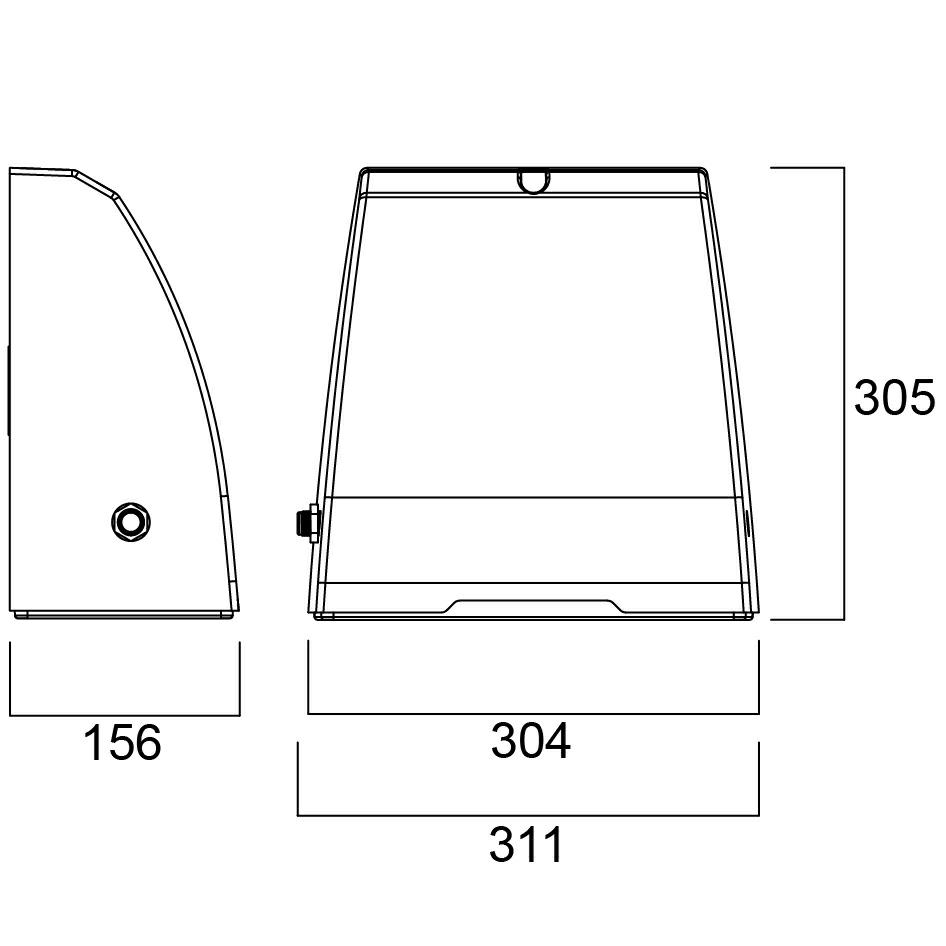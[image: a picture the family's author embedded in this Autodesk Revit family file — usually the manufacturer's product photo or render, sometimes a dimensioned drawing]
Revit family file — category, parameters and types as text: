
# Revit family: 0049944_3150lm
name_source: partatom
category: Lighting Fixtures
revit_build: Autodesk Revit 2018 (Build: 20170223_1515(x64)
units: mm (PartAtom-declared; Revit-internal decimal feet)

## family parameters
Cut with Voids When Loaded = No
Host = Face
Light Source = Yes
OmniClass Number = 23.80.70.00
OmniClass Title = Lighting
Part Type = Normal
Room Calculation Point = No
Round Connector Dimension = Use Diameter
Shared = No

## types (1)
- 0049944 MURO SURF IP65 1700-3250LM 840 PH GR
    Apparent Load = 28 VA
    Assembly Code = D5020200
    AssetType = Fixed
    ClassificationName = Uniclass2015
    ClassificationValue = EF_70_80
    Color Filter = 16777215
    Cost = 0 $
    Default Elevation = 1219 mm
    Description = Muro Surface is a wall mounted fixture for exterior lighting applications. Comes with aluminium housing in RAL7016 anthracite grey colour, frosted PC diffuser, IP65, IK10, Class I, 4000K, non-dimmable multipower driver with 5 settings, 1700 / 1900 / 2750 / 3150 / 3250 lm, 14 / 16 / 24 / 27 / 28 W, up to 121 lm/W total system efficacy, switchable built in Mini photocell, CRI80, Asymmetrical beam, 119.000 hrs L70B50 lifespan, 304 x 305 x 155 mm (L x W x D) dimensions, 4.1 kg weight.
    Dimming Lamp Color Temperature Shift = <None>
    DocumentationLiterature = http://www.sylvania-lighting.com
    ElectricShockClassification = 116
    Emit Shape Visible in Rendering = No
    Emit from Circle Diameter = 610 mm
    IfcExportAs = Class I
    IfcExportType = IfcLightFixtureType
    ImpactProtectionIndex = IfcLightFixtureType
    IngressProtection = IfcLightFixtureType
    InputNominalFrequency = 4000
    InputVoltage = 0
    LampColourRenderingIndex = 16500
    LampColourTemperature = LED
    LampMacAdamStep = 80
    LampNominalLuminous = 4000 K
    LightOutputRatio = LED
    LuminaireType = 0
    ManufacturerName = 116 lm/W
    Material = Feilo Sylvania
    Material_1_SYL = <By Category>
    Material_2_SYL = <By Category>
    Material_3_SYL = <By Category>
    Material_4_SYL = <By Category>
    Model = Muro Surface IP65 1700-3250lm 840 PH Grey
    ModelNumber = 0049944
    ModelReference = Muro Surface IP65 1700-3250lm 840 PH Grey
    Name = Muro Surface IP65 1700-3250lm 840 PH Grey
    NominalDepth = 155 mm  [stored 0.50853 ft]
    NominalHeight = 305 mm  [stored 1.00066 ft]
    NominalLength = 155 mm  [stored 0.50853 ft]
    Photometric Web File = 0049944_3150lm.IES
    PowerConsumption = Lighting
    PowerFactor = 0.95
    Tilt Angle = -90.00°
    Type Image = <None>
    TypeName = Muro Surface IP65 1700-3250lm 840 PH Grey
    URL = 0.9
    Voltage = 0 V
    WarrantyDescription = http://www.sylvania-lighting.com

note: [stored X ft] marks values corroborated as IEEE doubles in the binary element streams (Revit-internal decimal feet)

## geometry (parser evidence)
native form markers: Sweep x1
no freeform markers — native parametric forms only
